# Revit family: Icon_Wiring Center_RFA
name_source: partatom
category: Data Devices
units: mm (PartAtom-declared; Revit-internal decimal feet)

## family parameters
Cut with Voids When Loaded = No
Host = Face
Maintain Annotation Orientation = No
Part Type = Normal
Room Calculation Point = No
Round Connector Dimension = Use Diameter
Shared = No

## types (1)
- Icon_Wiring Center_230V
    Ball Pressure Test = 75
    Body Material = Danfoss Plastic Dark Gray
    Control Polution Situation = Degree 2
    Default Elevation = 1219.2 mm  [stored 4 ft]
    Description = Main Controller and Room Thermostat
    H = 115 mm  [stored 0.377297 ft]
    IfcExportAs = IfcElectricApplianceType
    IfcExportType = Icon
    Input (Cooling) = External switch input (230 V rating)
    Input (Setback) = External switch input (230 V rating)
    L = 360 mm  [stored 1.1811 ft]
    LOD 200 = No
    LOD 350 = Yes
    Manufacturer = Danfoss
    Max Ambient Temperature = 50 °C
    Max Number of Actuators = 14
    Max Number of Thermostats = 8
    Min Ambient Temperature = 0 °C
    Model = 088U1040,088U1041,088U1042
    Model Type = Icon_Wiring Center_230V
    Number of Actuator Output = 14
    Output (Cooling) = 230 V when active
    Output (Setback) = 230 V when active
    Output Relay (Boiler) = Volt-free (Max. 2 A)
    Output Relay (Pump) = 230 V (Max. 100 W)
    Output Voltage to Actuators = 230 V AC
    Power Supply = 220-240 V AC
    R1 = 2 mm  [stored 0.00656168 ft]
    Rated Impulse Voltage = 4 kV
    URL = https://store.danfoss.com
    Voltage = 230 V
    W = 50 mm  [stored 0.164042 ft]
    Weight = 0.15 kg

note: source unit labels omitted for Ball Pressure Test — the stored unit's dimension contradicts the parameter name (converter mislabeling)

note: [stored X ft] marks values corroborated as IEEE doubles in the binary element streams (Revit-internal decimal feet)

## geometry (parser evidence)
native form markers: Sweep x2
no freeform markers — native parametric forms only
